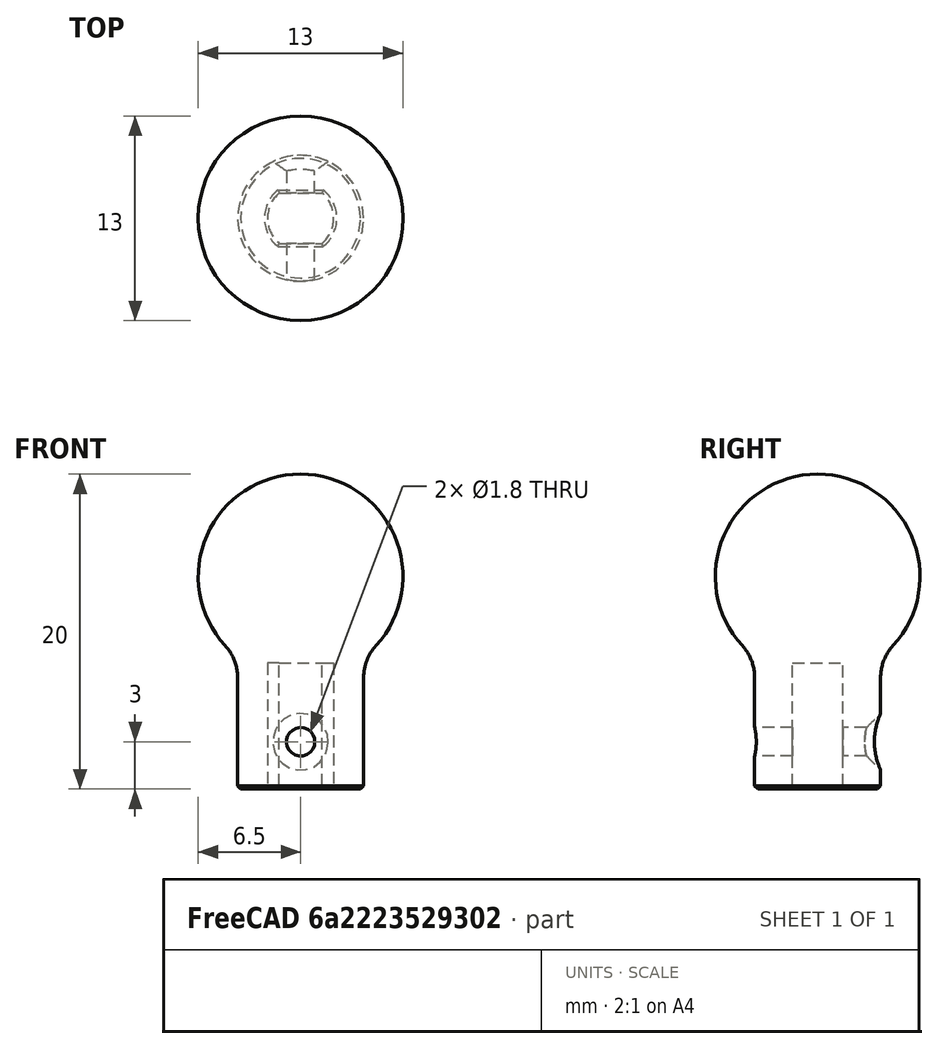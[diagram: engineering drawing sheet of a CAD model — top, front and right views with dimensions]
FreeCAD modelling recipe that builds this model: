
FCSTD DOCUMENT  (FreeCAD 0.21R33771 (Git))
Label: BallJoint13_SScrew
License: Creative Commons Attribution 4.0
LicenseURL: https://creativecommons.org/licenses/by/4.0/
objects: Sketcher::SketchObject×3, PartDesign::Pocket×2, PartDesign::Chamfer×2, Mesh::Feature×1, PartDesign::Revolution×1, PartDesign::Body×1
note: 14 computed .brp shape members not serialized (recipe doc carries the construction recipe); baked Part::Feature solids carry a one-line shape summary decoded from their .brp

FEATURE [Mesh::Feature] v3_ball_joint___B___tighter_motion_tolerance___13mm  label="v3-ball-joint - B - tighter motion tolerance - 13mm"
FEATURE [Sketcher::SketchObject] Sketch
  FullyConstrained = true
  MapMode = 5
  Placement = pos=(0,0,0) rot=(1,0,0;1.5708rad)
  Support = -> [XZ_Plane]
  sketch-geometry (6):
    g0: LineSegment StartX=0 StartY=0 StartZ=0 EndX=1.6e-15 EndY=20 EndZ=0
    g1: ArcOfCircle CenterX=-4e-16 CenterY=13.5 CenterZ=0 NormalX=0 NormalY=0 NormalZ=1 AngleXU=0 Radius=6.5 StartAngle=5.54078 EndAngle=7.85398
    g2: ArcOfCircle CenterX=7 CenterY=7.07738 CenterZ=0 NormalX=0 NormalY=0 NormalZ=1 AngleXU=0 Radius=3 StartAngle=2.39918 EndAngle=3.14159
    g3: LineSegment StartX=4 StartY=7.07738 StartZ=0 EndX=4 EndY=0.2 EndZ=0
    g4: LineSegment StartX=4 StartY=0.2 StartZ=0 EndX=3.8 EndY=0 EndZ=0
    g5: LineSegment StartX=3.8 StartY=0 StartZ=0 EndX=0 EndY=0 EndZ=0
  constraints (16):
    c: Coincident(g-1,g0)
    c: PointOnObject(g0,g-2)
    c: Perpendicular(g0,g1) = 1.5708
    c: Tangent(g1,g2) = 1.5708
    c: Tangent(g2,g3) = -1.5708
    c: Coincident(g3,g4)
    c: Coincident(g4,g5)
    c: Coincident(g5,g0)
    c: Horizontal(g5)
    c: Vertical(g3)
    c: Angle(g4,g5) = 2.35619
    c: DistanceY(g4,g3) = 0.2
    c: DistanceX(g0,g3) = 4
    c: DistanceY(g0,g0) = 20
    c: Radius(g1) = 6.5
    c: Radius(g2) = 3
FEATURE [PartDesign::Revolution] Revolution
  Angle = 360
  Axis = (0,2e-16,1)
  Base = (0,0,0)
  Placement = pos=(0,0,0) rot=(1,0,0;1.5708rad)
  Profile = -> Sketch
  ReferenceAxis = -> Sketch [V_Axis]
  Refine = true
  Reversed = true
FEATURE [Sketcher::SketchObject] Sketch001
  FullyConstrained = true
  MapMode = 5
  Support = -> [XY_Plane]
  sketch-geometry (4):
    g0: ArcOfCircle CenterX=0 CenterY=0 CenterZ=0 NormalX=0 NormalY=0 NormalZ=1 AngleXU=0 Radius=2.1 StartAngle=2.27534 EndAngle=4.00784
    g1: ArcOfCircle CenterX=0 CenterY=0 CenterZ=0 NormalX=0 NormalY=0 NormalZ=1 AngleXU=0 Radius=2.1 StartAngle=5.41694 EndAngle=7.14943
    g2: LineSegment StartX=-1.36015 StartY=1.6 StartZ=0 EndX=1.36015 EndY=1.6 EndZ=0
    g3: LineSegment StartX=-1.36015 StartY=-1.6 StartZ=0 EndX=1.36015 EndY=-1.6 EndZ=0
  constraints (11):
    c: Coincident(g0,g-1)
    c: Coincident(g1,g0)
    c: Coincident(g2,g0)
    c: Coincident(g2,g1)
    c: Horizontal(g2)
    c: Coincident(g3,g0)
    c: Coincident(g3,g1)
    c: Horizontal(g3)
    c: Symmetric(g0,g1,g0)
    c: DistanceY(g0,g0) = 3.2
    c: Diameter(g1) = 4.2
FEATURE [PartDesign::Pocket] Pocket
  BaseFeature = -> Revolution
  Direction = (0,0,-1)
  Length = 8
  Length2 = 5
  Placement = pos=(0,0,0) rot=(1,0,0;1.5708rad)
  Profile = -> Sketch001
  ReferenceAxis = -> Sketch001 [N_Axis]
  Refine = true
  Reversed = true
  Type = 0
FEATURE [Sketcher::SketchObject] Sketch002
  FullyConstrained = true
  MapMode = 5
  Placement = pos=(0,0,0) rot=(1,0,0;1.5708rad)
  Support = -> [XZ_Plane]
  sketch-geometry (1):
    g0: Circle CenterX=0 CenterY=3 CenterZ=0 NormalX=0 NormalY=0 NormalZ=1 AngleXU=0 Radius=0.9
  constraints (3):
    c: PointOnObject(g0,g-2)
    c: Diameter(g0) = 1.8
    c: DistanceY(g-1,g0) = 3
FEATURE [PartDesign::Pocket] Pocket001
  BaseFeature = -> Pocket
  Direction = (0,1,2e-16)
  Length = 5
  Length2 = 5
  Midplane = true
  Placement = pos=(0,0,0) rot=(1,0,0;1.5708rad)
  Profile = -> Sketch002
  ReferenceAxis = -> Sketch002 [N_Axis]
  Refine = true
  Type = 1
FEATURE [PartDesign::Chamfer] Chamfer
  Angle = 45
  Base = -> Pocket001 [Edge9]
  BaseFeature = -> Pocket001
  ChamferType = 0
  FlipDirection = false
  Placement = pos=(0,0,0) rot=(1,0,0;1.5708rad)
  Refine = true
  Size = 0.9
  Size2 = 1
  SupportTransform = false
  UseAllEdges = false
FEATURE [PartDesign::Chamfer] Chamfer001
  Angle = 45
  Base = -> Chamfer [Edge17,Edge18,Edge16,Edge19]
  BaseFeature = -> Chamfer
  ChamferType = 0
  FlipDirection = false
  Placement = pos=(0,0,0) rot=(1,0,0;1.5708rad)
  Refine = true
  Size = 0.2
  Size2 = 1
  SupportTransform = false
  UseAllEdges = false
FEATURE [PartDesign::Body] Body  label="BallJoint13_SScrew"
  Group = -> [Sketch,Revolution,Sketch001,Pocket,Sketch002,Pocket001,Chamfer,Chamfer001]
  Origin = -> Origin
  Tip = -> Chamfer001
